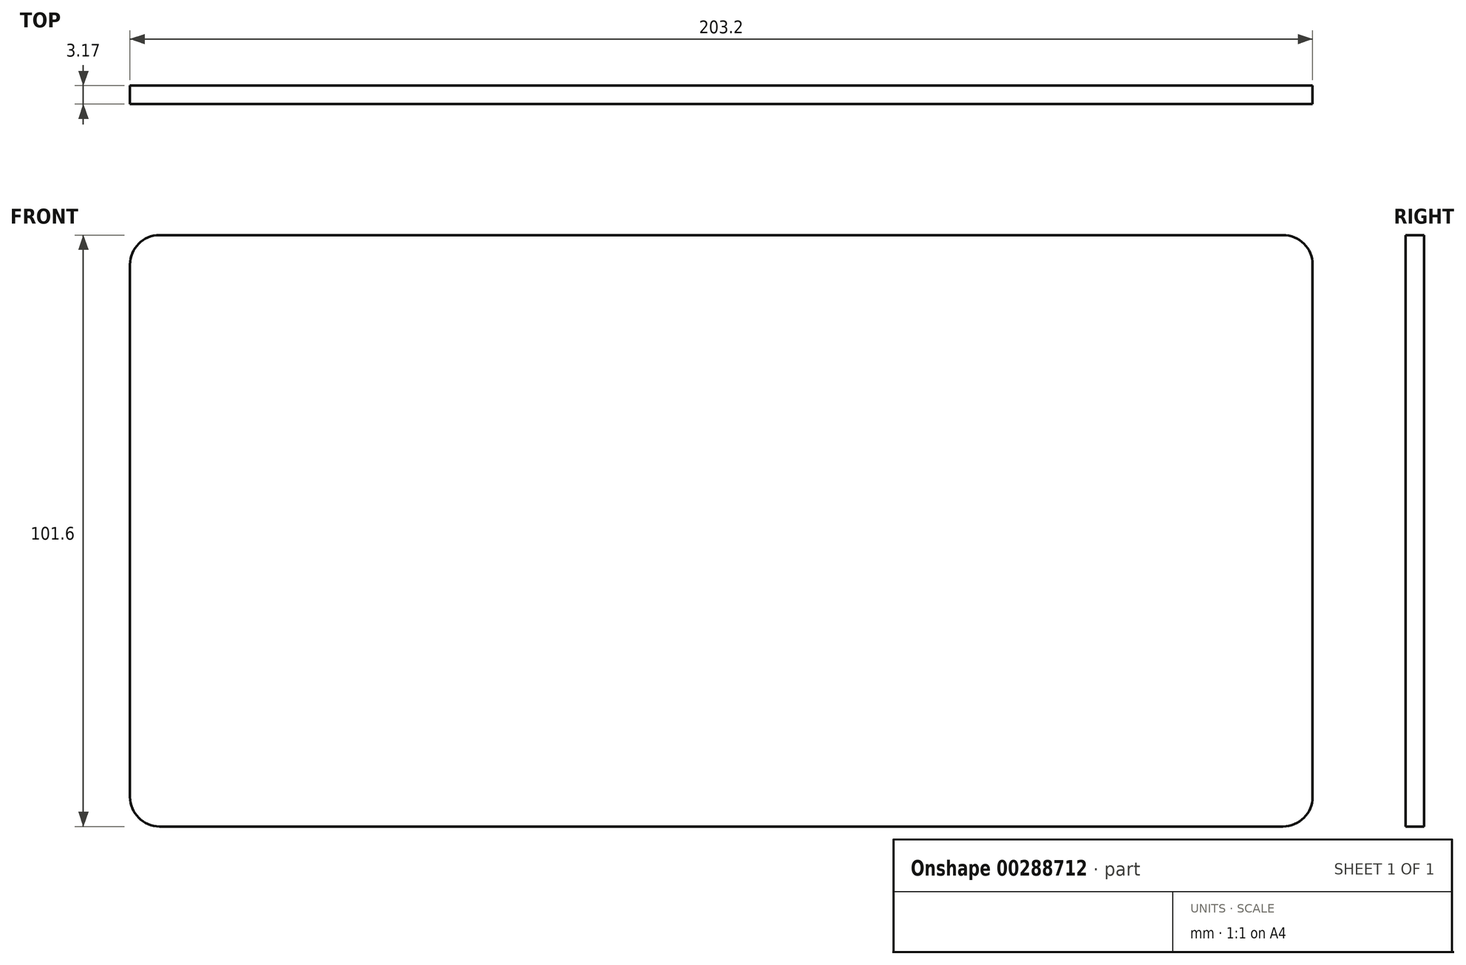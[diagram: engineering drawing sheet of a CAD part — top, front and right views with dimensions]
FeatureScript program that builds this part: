
annotation { "Feature Type Name" : "Feature", "Feature Type Description" : "" }
export const myFeature = defineFeature(function(context is Context, id is Id, definition is map)
    precondition{}
    {
        {
            var Q0;
            Q0=qCreatedBy(makeId("Front.planeOp"),FACE);
            var sketch = newSketch(context, id + "F0", { "sketchPlane" : qUnion([Q0])});
            skLineSegment(sketch, "E0.bottom", {"start": v(101.6, -50.8) * mm, "end": v(-101.6, -50.8) * mm});
            skLineSegment(sketch, "E0.top", {"start": v(101.6, 50.8) * mm, "end": v(-101.6, 50.8) * mm});
            skLineSegment(sketch, "E0.left", {"start": v(101.6, -50.8) * mm, "end": v(101.6, 50.8) * mm});
            skLineSegment(sketch, "E0.right", {"start": v(-101.6, -50.8) * mm, "end": v(-101.6, 50.8) * mm});
            skPoint(sketch, "E0.middle", {"position": v(0, 0) * mm});
            skSolve(sketch);
        }
        {
            var Q0;
            Q0=makeQuery(id+"F0.imprint","IMPRINT",FACE,{"disambiguationData":[TD([[makeQuery(id+"F0.imprint","IMPRINT",EDGE,{"derivedFrom":sQuery(id+"F0.wireOp",EDGE,"E0.bottom")}),-1.0]])]});
            extrude(context, id + "F1", {"entities" : qUnion([Q0]), "depth" : 3.17 * mm});
        }
        {
            var Q0;
            Q0=makeQuery(id+"F1.opExtrude","SWEPT_EDGE",EDGE,{"disambiguationData":[OSD([sQuery(id+"F0.wireOp",EDGE,"E0.top"),sQuery(id+"F0.wireOp",EDGE,"E0.right")])]});
            var Q1;
            Q1=makeQuery(id+"F1.opExtrude","SWEPT_EDGE",EDGE,{"disambiguationData":[OSD([sQuery(id+"F0.wireOp",EDGE,"E0.bottom"),sQuery(id+"F0.wireOp",EDGE,"E0.right")])]});
            var Q2;
            Q2=makeQuery(id+"F1.opExtrude","SWEPT_EDGE",EDGE,{"disambiguationData":[OSD([sQuery(id+"F0.wireOp",EDGE,"E0.top"),sQuery(id+"F0.wireOp",EDGE,"E0.left")])]});
            var Q3;
            Q3=makeQuery(id+"F1.opExtrude","SWEPT_EDGE",EDGE,{"disambiguationData":[OSD([sQuery(id+"F0.wireOp",EDGE,"E0.bottom"),sQuery(id+"F0.wireOp",EDGE,"E0.left")])]});
            fillet(context, id + "F2", {"entities" : qUnion([Q0, Q1, Q2, Q3]), "radius" : 5.08 * mm, "tangentPropagation" : true, "allowEdgeOverflow" : false});
        }
    });
